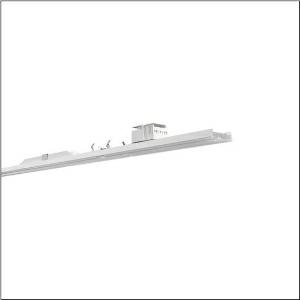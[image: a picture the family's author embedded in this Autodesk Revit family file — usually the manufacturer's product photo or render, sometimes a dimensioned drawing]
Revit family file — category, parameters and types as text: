
# Revit family: licross_r__11_recessed_mo_51tl18vn465f_2b29
name_source: partatom
category: Lighting Fixtures
units: mm (PartAtom-declared; Revit-internal decimal feet)

## family parameters
Cut with Voids When Loaded = No
Host = Face
Light Source = No
Part Type = Normal
Room Calculation Point = No
Round Connector Dimension = Use Diameter
Shared = No

## types (1)
- --- (1 x LED, 6520 lm, 39.6 W, 4000K)
    Apparent Load = 40 VA
    CIE Flux Codes = 83 96 99 100 100
    Color Rendering = 80
    Color Temperature = 4000K
    Default Elevation = 1800 mm
    Description = Licross® 11 Recessed MOluminaire insert, length: 1.500mm, width: 66mm, height: 67mm, LED rated luminous flux: 6.520lm, light colour: 840, control gear: DALI 2, CLO, control gear: ECG DALI, with plug, 5-pole, with phase selection, mains connection: 220..240V, AC, 50/60Hz, halogen-free wiring, primary optical cover: cover, of PMMA, light emission: direct distribution, protection rating (complete): IP40, insulation class (complete): insulation class I (protective earthing), certification: CE, ENEC, VDE, UKCA, protection symbol: D if used in an environment without relevant dust loads with corresponding accessories, permissible ambient temperature for indoor applications: -25..+40°C, corresponds to IFS (International Featured Standards) requirements for safety and quality in the food industry, reducing of maximum allowable ambient temperature of 5°C with ceiling mounting, packaging unit: 1 piece
    Height = 58 mm
    Lamp = 1 x LED
    Lamp Light Flux = 6520 lm
    Lamp Power = 39.6 W
    Lamp count = 1
    Length = 1500 mm
    Luminous efficacy = 165 lm/W
    Manufacturer = Siteco
    ModVariant = No
    Model = 51TL18VN465F
    Mounting Place = Ceiling
    Mounting Type = Pendant
    Number of Poles = 1
    OnlyDefault = Yes
    Power Factor = 1
    Product Name = Licross® 11 Recessed MO
    Product group = luminaire insert
    ProductGroupID = 902
    Protection Class = Protection class I
    Protection Degree = IP 40
    RLX_Detail_Level = 1
    RlxData = <blob elided: 22337 chars, md5=c4b59dbc>
    Socket = socket
    Standby Power = 0 W
    System Light Flux = 6520 lm
    System Power = 40 W
    Type Comments = factory setting: luminous flux: 100 % | dim-lin: 254 | 261 mA
    Type Image = l_1266722.jpg
    URL = http://relux.com
    VarID = @adj_129071
    Voltage = 0 V
    Weight = 0.00 kg
    Width = 66 mm

## geometry (parser evidence)
native form markers: Blend x4, Sweep x11
no freeform markers — native parametric forms only
